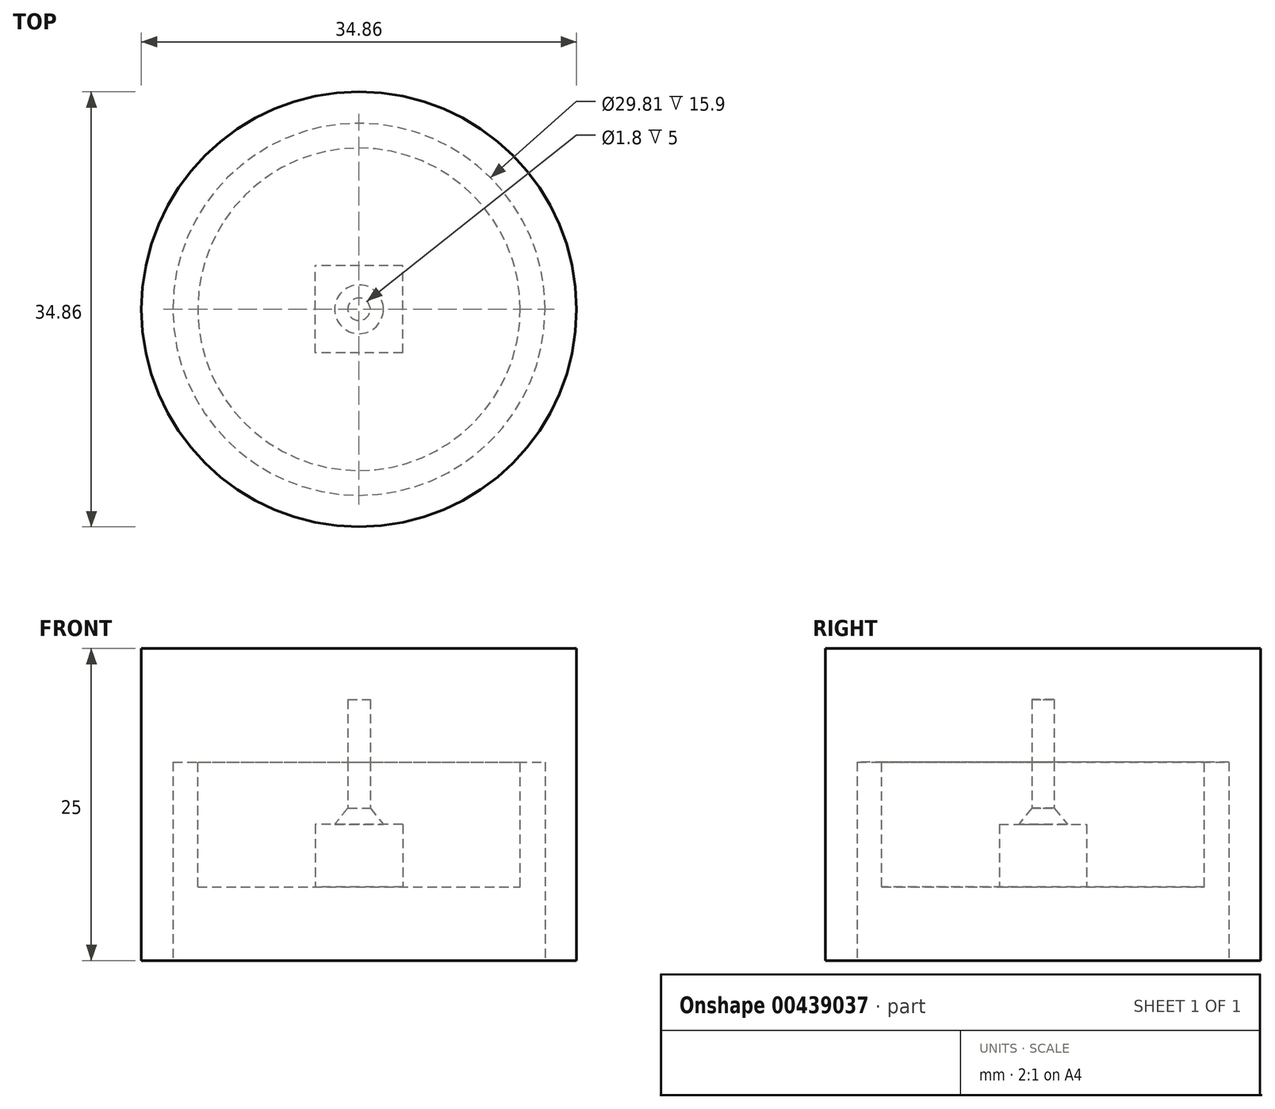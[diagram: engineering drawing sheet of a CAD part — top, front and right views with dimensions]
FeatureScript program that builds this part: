
annotation { "Feature Type Name" : "Feature", "Feature Type Description" : "" }
export const myFeature = defineFeature(function(context is Context, id is Id, definition is map)
    precondition{}
    {
        {
            var Q0;
            Q0=qCreatedBy(makeId("Top.planeOp"),FACE);
            var sketch = newSketch(context, id + "F0", { "sketchPlane" : qUnion([Q0])});
            skCircle(sketch, "E0", {"center": v(0, 0) * mm, "radius": 17.43 * mm});
            skSolve(sketch);
        }
        {
            var Q0;
            Q0=qSketchRegion(id+"F0",true);
            extrude(context, id + "F1", {"entities" : qUnion([Q0]), "depth" : 25 * mm});
        }
        {
            var Q0;
            Q0=makeQuery(id+"F1.opExtrude","CAP_FACE",FACE,{"disambiguationData":[OSD([sQuery(id+"F0.wireOp",EDGE,"E0")])],"isStart":true});
            var sketch = newSketch(context, id + "F2", { "sketchPlane" : qUnion([Q0])});
            skCircle(sketch, "E1", {"center": v(0, 0) * mm, "radius": 14.9 * mm});
            skSolve(sketch);
        }
        {
            var Q0;
            Q0=qSketchRegion(id+"F2",true);
            extrude(context, id + "F3", {"entities" : qUnion([Q0]), "operationType" : NewBodyOperationType.REMOVE, "oppositeDirection" : true, "depth" : 15.9 * mm});
        }
        {
            var Q0;
            Q0=makeQuery(id+"F3.boolean.opBoolean","COPY",FACE,{"derivedFrom":makeQuery(id+"F3.opExtrude","CAP_FACE",FACE,{"disambiguationData":[OSD([sQuery(id+"F2.wireOp",EDGE,"E1")])],"isStart":false})});
            var sketch = newSketch(context, id + "F4", { "sketchPlane" : qUnion([Q0])});
            skCircle(sketch, "E2", {"center": v(0, 0) * mm, "radius": 0.9 * mm});
            skSolve(sketch);
        }
        {
            var Q0;
            Q0=qSketchRegion(id+"F4",true);
            extrude(context, id + "F5", {"entities" : qUnion([Q0]), "operationType" : NewBodyOperationType.REMOVE, "oppositeDirection" : true, "depth" : 5 * mm});
        }
        {
            var Q0;
            Q0=makeQuery(id+"F3.boolean.opBoolean","COPY",FACE,{"derivedFrom":makeQuery(id+"F3.opExtrude","CAP_FACE",FACE,{"disambiguationData":[OSD([sQuery(id+"F2.wireOp",EDGE,"E1")])],"isStart":false})});
            var sketch = newSketch(context, id + "F6", { "sketchPlane" : qUnion([Q0])});
            skCircle(sketch, "E3", {"center": v(0, 0) * mm, "radius": 12.92 * mm});
            skSolve(sketch);
        }
        {
            var Q0;
            Q0=qSketchRegion(id+"F6",true);
            extrude(context, id + "F7", {"entities" : qUnion([Q0]), "depth" : 10 * mm});
        }
        {
            var Q0;
            Q0=makeQuery(id+"F7.opExtrude","CAP_FACE",FACE,{"disambiguationData":[OSD([sQuery(id+"F6.wireOp",EDGE,"E3")])],"isStart":false});
            var sketch = newSketch(context, id + "F8", { "sketchPlane" : qUnion([Q0])});
            skCircle(sketch, "E4", {"center": v(0, 0) * mm, "radius": 1.34 * mm});
            skSolve(sketch);
        }
        {
            var Q0;
            Q0=makeQuery(id+"F8.imprint","IMPRINT",FACE,{"disambiguationData":[TD([[makeQuery(id+"F8.imprint","IMPRINT",EDGE,{"derivedFrom":sQuery(id+"F8.wireOp",EDGE,"E4")}),-1.0]])]});
            var sketch = newSketch(context, id + "F9", { "sketchPlane" : qUnion([Q0])});
            skLineSegment(sketch, "E5.bottom", {"start": v(3.5, 3.5) * mm, "end": v(-3.5, 3.5) * mm});
            skLineSegment(sketch, "E5.top", {"start": v(3.5, -3.5) * mm, "end": v(-3.5, -3.5) * mm});
            skLineSegment(sketch, "E5.left", {"start": v(3.5, 3.5) * mm, "end": v(3.5, -3.5) * mm});
            skLineSegment(sketch, "E5.right", {"start": v(-3.5, 3.5) * mm, "end": v(-3.5, -3.5) * mm});
            skPoint(sketch, "E5.middle", {"position": v(0, 0) * mm});
            skSolve(sketch);
        }
        {
            var Q0;
            Q0=qSketchRegion(id+"F9",true);
            extrude(context, id + "F10", {"entities" : qUnion([Q0]), "operationType" : NewBodyOperationType.REMOVE, "oppositeDirection" : true, "depth" : 5 * mm});
        }
        {
            var Q0;
            Q0=sQuery(id+"F8.wireOp",VERTEX,"E4.center");
            var Q1;
            Q1=makeQuery(id+"F7.opExtrude","SWEPT_BODY",BODY,{"disambiguationData":[OSD([sQuery(id+"F6.wireOp",EDGE,"E3")])]});
            hole(context, id + "F11", {"style" : HoleStyle.C_SINK, "endStyle" : HoleEndStyle.BLIND, "holeDiameter" : 1.8 * mm, "cSinkDiameter" : 3.9 * mm, "cSinkAngle" : 76.73 * degree, "holeDepth" : 5 * mm, "tappedDepth" : 12 * mm, "tapClearance" : 3, "locations" : qUnion([Q0]), "scope" : qUnion([Q1])});
        }
    });
